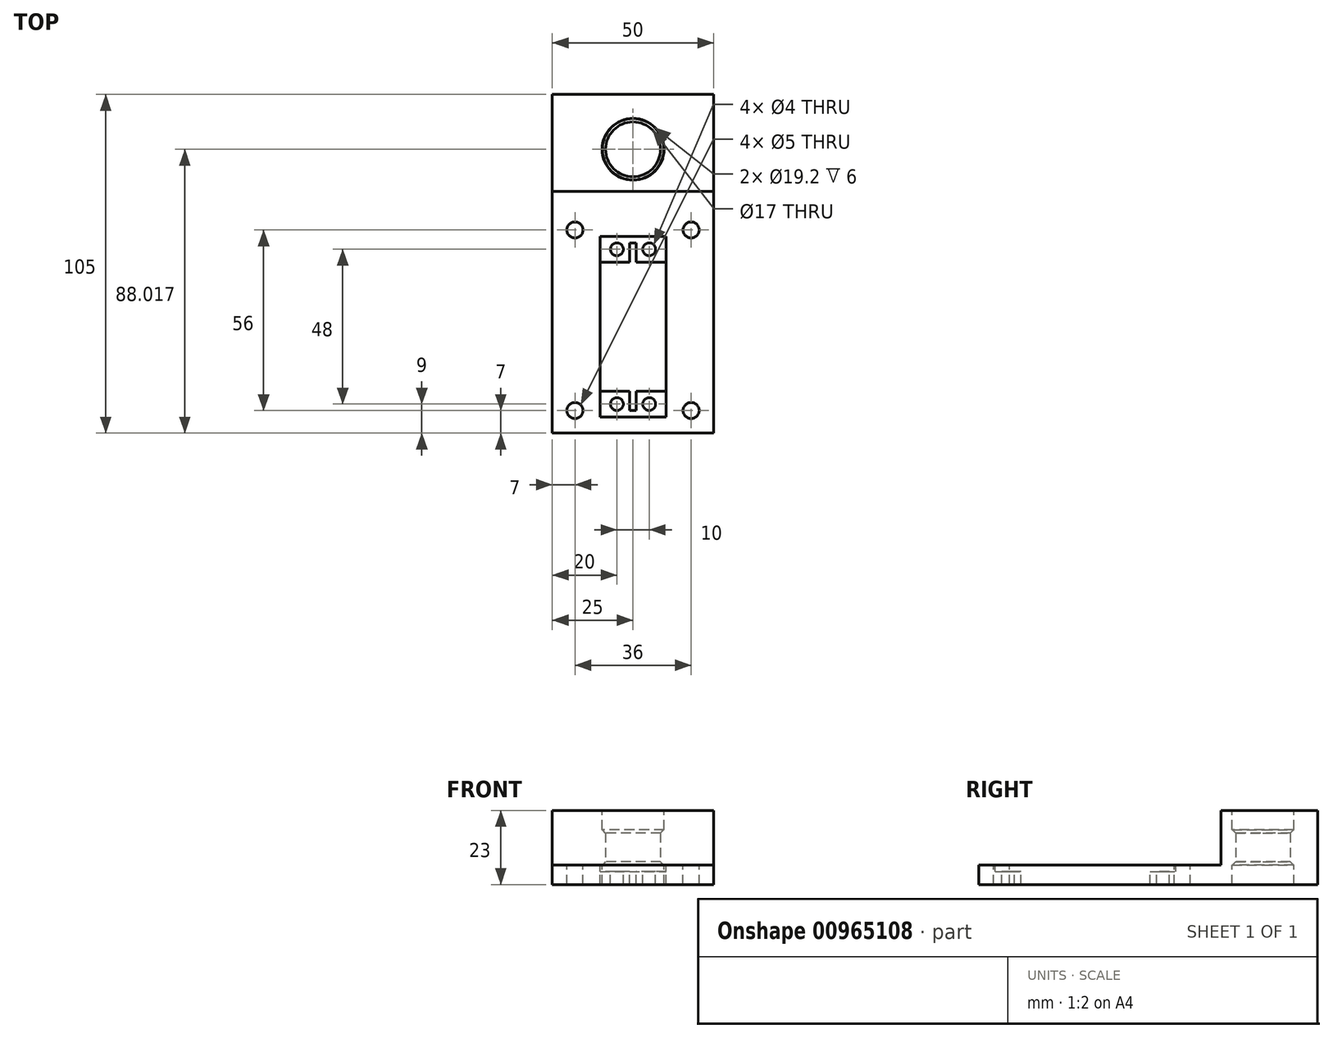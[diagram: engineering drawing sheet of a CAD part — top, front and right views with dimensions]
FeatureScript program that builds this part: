
annotation { "Feature Type Name" : "Feature", "Feature Type Description" : "" }
export const myFeature = defineFeature(function(context is Context, id is Id, definition is map)
    precondition{}
    {
        {
            var Q0;
            Q0=qCreatedBy(makeId("Top.planeOp"),FACE);
            var sketch = newSketch(context, id + "F0", { "sketchPlane" : qUnion([Q0])});
            skLineSegment(sketch, "E0.bottom", {"start": v(0, 0) * mm, "end": v(50, 0) * mm});
            skLineSegment(sketch, "E0.top", {"start": v(0, 105) * mm, "end": v(50, 105) * mm});
            skLineSegment(sketch, "E0.left", {"start": v(0, 0) * mm, "end": v(0, 105) * mm});
            skLineSegment(sketch, "E0.right", {"start": v(50, 0) * mm, "end": v(50, 105) * mm});
            skLineSegment(sketch, "E1.bottom", {"start": v(14.75, 5) * mm, "end": v(35.25, 5) * mm});
            skLineSegment(sketch, "E1.top", {"start": v(14.75, 61) * mm, "end": v(35.25, 61) * mm});
            skLineSegment(sketch, "E1.left", {"start": v(14.75, 5) * mm, "end": v(14.75, 61) * mm});
            skLineSegment(sketch, "E1.right", {"start": v(35.25, 5) * mm, "end": v(35.25, 61) * mm});
            skLineSegment(sketch, "E2", {"start": v(35.25, 53) * mm, "end": v(14.75, 53) * mm});
            skLineSegment(sketch, "E3", {"start": v(35.25, 13) * mm, "end": v(14.75, 13) * mm});
            skCircle(sketch, "E4", {"center": v(20, 57) * mm, "radius": 2 * mm});
            skCircle(sketch, "E5", {"center": v(30, 57) * mm, "radius": 2 * mm});
            skCircle(sketch, "E6", {"center": v(20, 9) * mm, "radius": 2 * mm});
            skCircle(sketch, "E7", {"center": v(30, 9) * mm, "radius": 2 * mm});
            skCircle(sketch, "E8", {"center": v(7, 63) * mm, "radius": 2.5 * mm});
            skCircle(sketch, "E9", {"center": v(43, 63) * mm, "radius": 2.5 * mm});
            skCircle(sketch, "E10", {"center": v(7, 7) * mm, "radius": 2.5 * mm});
            skCircle(sketch, "E11", {"center": v(43, 7) * mm, "radius": 2.5 * mm});
            skLineSegment(sketch, "E12.bottom", {"start": v(26, 53) * mm, "end": v(24, 53) * mm});
            skLineSegment(sketch, "E12.top", {"start": v(26, 59) * mm, "end": v(24, 59) * mm});
            skLineSegment(sketch, "E12.left", {"start": v(26, 53) * mm, "end": v(26, 59) * mm});
            skLineSegment(sketch, "E12.right", {"start": v(24, 53) * mm, "end": v(24, 59) * mm});
            skLineSegment(sketch, "E13.bottom", {"start": v(24, 13) * mm, "end": v(26, 13) * mm});
            skLineSegment(sketch, "E13.top", {"start": v(24, 7) * mm, "end": v(26, 7) * mm});
            skLineSegment(sketch, "E13.left", {"start": v(24, 13) * mm, "end": v(24, 7) * mm});
            skLineSegment(sketch, "E13.right", {"start": v(26, 13) * mm, "end": v(26, 7) * mm});
            skPoint(sketch, "E14", {"position": v(25, 43) * mm});
            skPoint(sketch, "E15", {"position": v(25, 88.02) * mm});
            skCircle(sketch, "E16", {"center": v(25, 88.02) * mm, "radius": 9.6 * mm});
            skLineSegment(sketch, "E17.top", {"start": v(0, 75) * mm, "end": v(50, 75) * mm});
            skLineSegment(sketch, "E17.left", {"start": v(0, 105) * mm, "end": v(0, 75) * mm});
            skLineSegment(sketch, "E17.right", {"start": v(50, 105) * mm, "end": v(50, 75) * mm});
            skCircle(sketch, "E18", {"center": v(25, 88.02) * mm, "radius": 8.5 * mm});
            skSolve(sketch);
        }
        {
            var Q0;
            Q0=makeQuery(id+"F0.imprint","IMPRINT",FACE,{"disambiguationData":[TD([[makeQuery(id+"F0.imprint","IMPRINT",EDGE,{"derivedFrom":sQuery(id+"F0.wireOp",EDGE,"E0.bottom")}),1.0]])]});
            var Q1;
            {var subQ2=sQuery(id+"F0.wireOp",EDGE,"E1.top");Q1=makeQuery(id+"F0.imprint","IMPRINT",FACE,{"disambiguationData":[TD([[makeQuery(id+"F0.imprint","IMPRINT",EDGE,{"derivedFrom":subQ2}),-1.0]])]});}
            var Q2;
            {var subQ2=sQuery(id+"F0.wireOp",EDGE,"E1.bottom");Q2=makeQuery(id+"F0.imprint","IMPRINT",FACE,{"disambiguationData":[TD([[makeQuery(id+"F0.imprint","IMPRINT",EDGE,{"derivedFrom":subQ2}),1.0]])]});}
            var Q3;
            Q3=makeQuery(id+"F0.imprint","IMPRINT",FACE,{"disambiguationData":[TD([[makeQuery(id+"F0.imprint","IMPRINT",EDGE,{"derivedFrom":sQuery(id+"F0.wireOp",EDGE,"E16")}),-1.0]])]});
            extrude(context, id + "F1", {"entities" : qUnion([Q0, Q1, Q2, Q3]), "oppositeDirection" : true, "depth" : 6 * mm, "offsetDistance" : 25 * mm});
        }
        {
            var Q0;
            {var subQ2=sQuery(id+"F0.wireOp",EDGE,"E1.top");Q0=makeQuery(id+"F0.imprint","IMPRINT",FACE,{"disambiguationData":[TD([[makeQuery(id+"F0.imprint","IMPRINT",EDGE,{"derivedFrom":subQ2}),-1.0]])]});}
            var Q1;
            {var subQ2=sQuery(id+"F0.wireOp",EDGE,"E1.bottom");Q1=makeQuery(id+"F0.imprint","IMPRINT",FACE,{"disambiguationData":[TD([[makeQuery(id+"F0.imprint","IMPRINT",EDGE,{"derivedFrom":subQ2}),1.0]])]});}
            extrude(context, id + "F2", {"entities" : qUnion([Q0, Q1]), "operationType" : NewBodyOperationType.REMOVE, "oppositeDirection" : true, "depth" : 2 * mm, "offsetDistance" : 25 * mm});
        }
        {
            var Q0;
            Q0=makeQuery(id+"F0.imprint","IMPRINT",FACE,{"disambiguationData":[TD([[makeQuery(id+"F0.imprint","IMPRINT",EDGE,{"derivedFrom":sQuery(id+"F0.wireOp",EDGE,"E16")}),-1.0]])]});
            extrude(context, id + "F3", {"entities" : qUnion([Q0]), "operationType" : NewBodyOperationType.ADD, "depth" : 17 * mm, "offsetDistance" : 25 * mm});
        }
        {
            var Q0;
            Q0=makeQuery(id+"F0.imprint","IMPRINT",FACE,{"disambiguationData":[TD([[makeQuery(id+"F0.imprint","IMPRINT",EDGE,{"derivedFrom":sQuery(id+"F0.wireOp",EDGE,"E16")}),1.0]])]});
            extrude(context, id + "F4", {"entities" : qUnion([Q0]), "operationType" : NewBodyOperationType.ADD, "depth" : 11 * mm, "offsetDistance" : 25 * mm});
        }
        {
            var Q0;
            Q0=makeQuery(id+"F4.opExtrude","CAP_EDGE",EDGE,{"disambiguationData":[OSD([sQuery(id+"F0.wireOp",EDGE,"E18")])],"isStart":false});
            var Q1;
            Q1=makeQuery(id+"F4.opExtrude","CAP_EDGE",EDGE,{"disambiguationData":[OSD([sQuery(id+"F0.wireOp",EDGE,"E18")])],"isStart":true});
            chamfer(context, id + "F5", {"entities" : qUnion([Q0, Q1]), "width" : 1 * mm, "tangentPropagation" : true});
        }
    });
